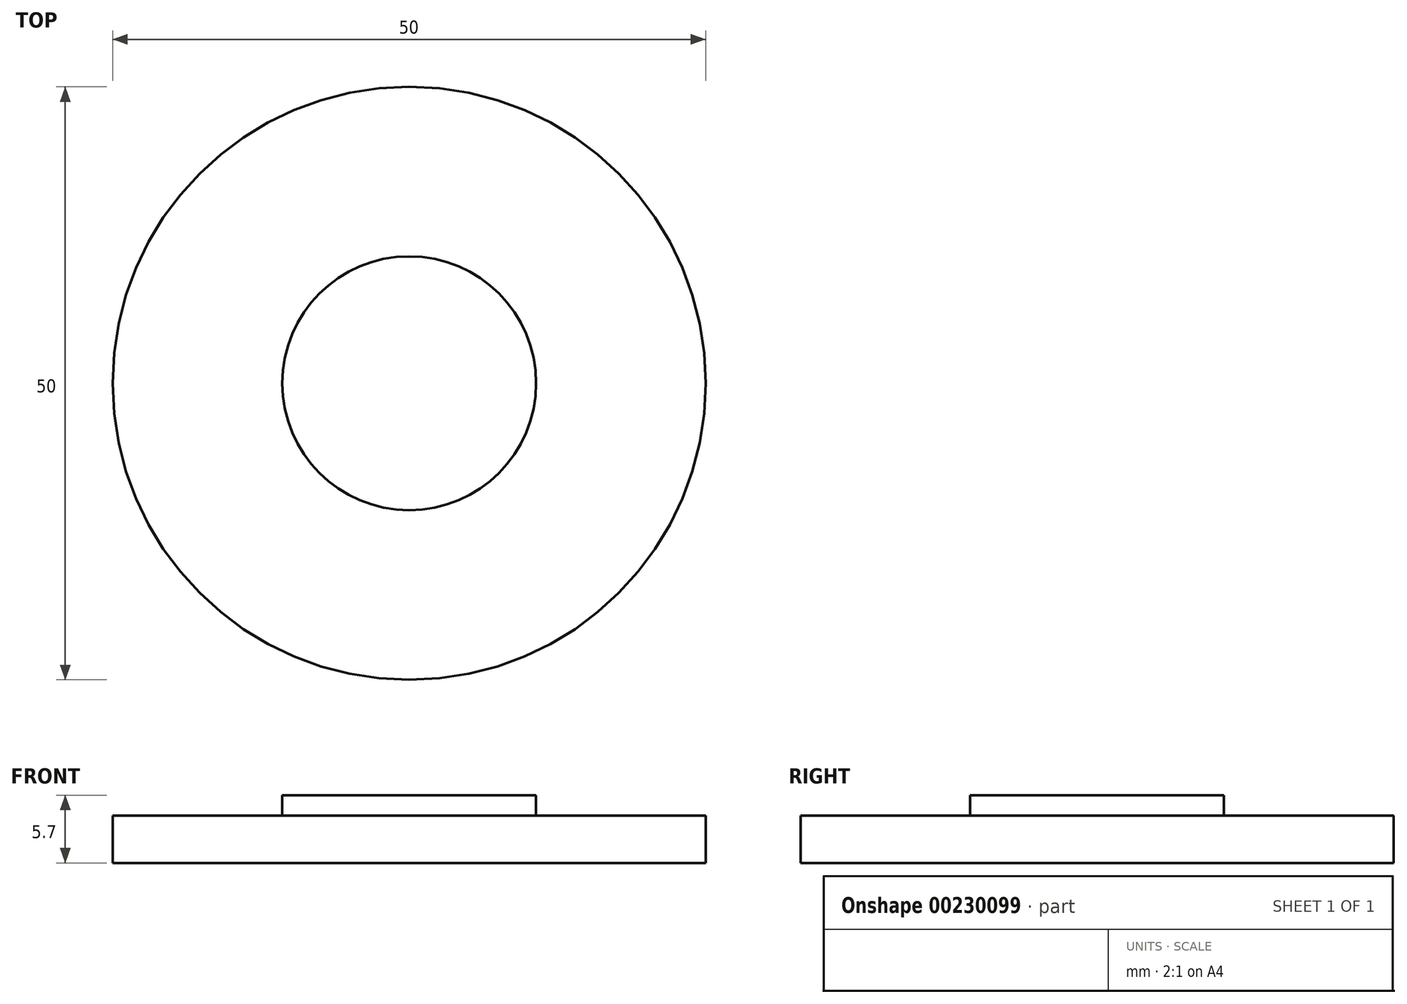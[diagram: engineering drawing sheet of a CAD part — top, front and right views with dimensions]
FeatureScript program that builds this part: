
annotation { "Feature Type Name" : "Feature", "Feature Type Description" : "" }
export const myFeature = defineFeature(function(context is Context, id is Id, definition is map)
    precondition{}
    {
        {
            var Q0;
            Q0=qCreatedBy(makeId("Top.planeOp"),FACE);
            var sketch = newSketch(context, id + "F0", { "sketchPlane" : qUnion([Q0])});
            skCircle(sketch, "E0", {"center": v(0, 0) * mm, "radius": 10.7 * mm});
            skCircle(sketch, "E1", {"center": v(0, 0) * mm, "radius": 25 * mm});
            skSolve(sketch);
        }
        {
            var Q0;
            Q0=makeQuery(id+"F0.imprint","IMPRINT",FACE,{"disambiguationData":[TD([[makeQuery(id+"F0.imprint","IMPRINT",EDGE,{"derivedFrom":sQuery(id+"F0.wireOp",EDGE,"E0")}),-1.0]])]});
            extrude(context, id + "F1", {"entities" : qUnion([Q0]), "depth" : 4 * mm, "offsetDistance" : 25 * mm});
        }
        {
            var Q0;
            Q0=makeQuery(id+"F0.imprint","IMPRINT",FACE,{"disambiguationData":[TD([[makeQuery(id+"F0.imprint","IMPRINT",EDGE,{"derivedFrom":sQuery(id+"F0.wireOp",EDGE,"E0")}),1.0]])]});
            extrude(context, id + "F2", {"entities" : qUnion([Q0]), "operationType" : NewBodyOperationType.ADD, "depth" : 5.7 * mm, "offsetDistance" : 25 * mm});
        }
    });
